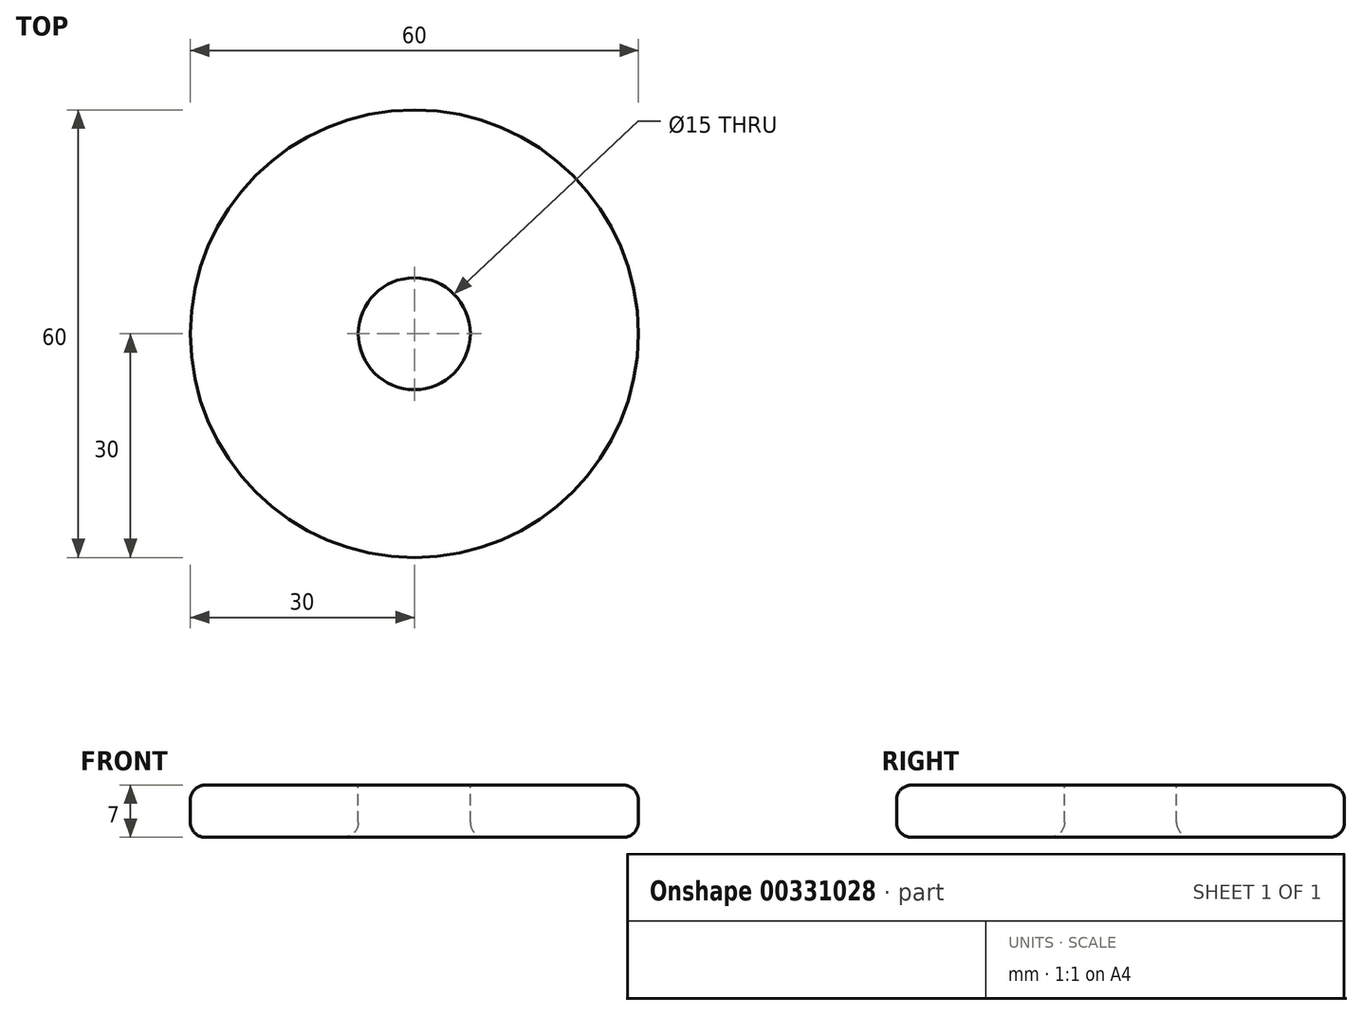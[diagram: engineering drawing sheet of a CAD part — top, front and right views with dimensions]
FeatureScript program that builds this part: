
annotation { "Feature Type Name" : "Feature", "Feature Type Description" : "" }
export const myFeature = defineFeature(function(context is Context, id is Id, definition is map)
    precondition{}
    {
        {
            var Q0;
            Q0=qCreatedBy(makeId("Top.planeOp"),FACE);
            var sketch = newSketch(context, id + "F0", { "sketchPlane" : qUnion([Q0])});
            skCircle(sketch, "E0", {"center": v(0, 0) * mm, "radius": 30 * mm});
            skSolve(sketch);
        }
        {
            var Q0;
            Q0 = qSketchRegion(id + "F0", true);
            extrude(context, id + "F1", {"entities" : qUnion([Q0]), "depth" : 7 * mm});
        }
        {
            var Q0;
            Q0=makeQuery(id+"F1.opExtrude","CAP_FACE",FACE,{"disambiguationData":[OSD([sQuery(id+"F0.wireOp",EDGE,"E0")])],"isStart":false});
            var sketch = newSketch(context, id + "F2", { "sketchPlane" : qUnion([Q0])});
            skSolve(sketch);
        }
        {
            var Q0;
            Q0=makeQuery(id+"F2.imprint","IMPRINT",FACE,{"disambiguationData":[TD([[makeQuery(id+"F2.imprint","IMPRINT",EDGE,{"derivedFrom":makeQuery(id+"F1.opExtrude","CAP_EDGE",EDGE,{"disambiguationData":[OSD([sQuery(id+"F0.wireOp",EDGE,"E0")])],"isStart":false})}),1.0]])]});
            var sketch = newSketch(context, id + "F3", { "sketchPlane" : qUnion([Q0])});
            skCircle(sketch, "E1", {"center": v(0, 0) * mm, "radius": 7.5 * mm});
            skSolve(sketch);
        }
        {
            var Q0;
            Q0 = qSketchRegion(id + "F3", true);
            extrude(context, id + "F4", {"entities" : qUnion([Q0]), "operationType" : NewBodyOperationType.REMOVE, "oppositeDirection" : true, "depth" : 25 * mm});
        }
        {
            var Q0;
            Q0=makeQuery(id+"F4.boolean.opBoolean","COPY",EDGE,{"derivedFrom":makeQuery(id+"F4.opExtrude","CAP_EDGE",EDGE,{"disambiguationData":[OSD([sQuery(id+"F3.wireOp",EDGE,"E1")])],"isStart":true})});
            var Q1;
            Q1=makeQuery(id+"F4.boolean.opBoolean","INTERSECT",EDGE,{"derivedFrom":[makeQuery(id+"F1.opExtrude","CAP_FACE",FACE,{"disambiguationData":[OSD([sQuery(id+"F0.wireOp",EDGE,"E0")])],"isStart":true}),makeQuery(id+"F4.opExtrude","SWEPT_FACE",FACE,{"disambiguationData":[OSD([sQuery(id+"F3.wireOp",EDGE,"E1")])]})]});
            fillet(context, id + "F5", {"entities" : qUnion([Q0, Q1]), "radius" : 2 * mm, "tangentPropagation" : true, "allowEdgeOverflow" : false});
        }
        {
            var Q0;
            Q0=makeQuery(id+"F1.opExtrude","CAP_EDGE",EDGE,{"disambiguationData":[OSD([sQuery(id+"F0.wireOp",EDGE,"E0")])],"isStart":false});
            var Q1;
            Q1=makeQuery(id+"F1.opExtrude","CAP_EDGE",EDGE,{"disambiguationData":[OSD([sQuery(id+"F0.wireOp",EDGE,"E0")])],"isStart":true});
            fillet(context, id + "F6", {"entities" : qUnion([Q0, Q1]), "radius" : 2 * mm, "tangentPropagation" : true, "allowEdgeOverflow" : false});
        }
    });
